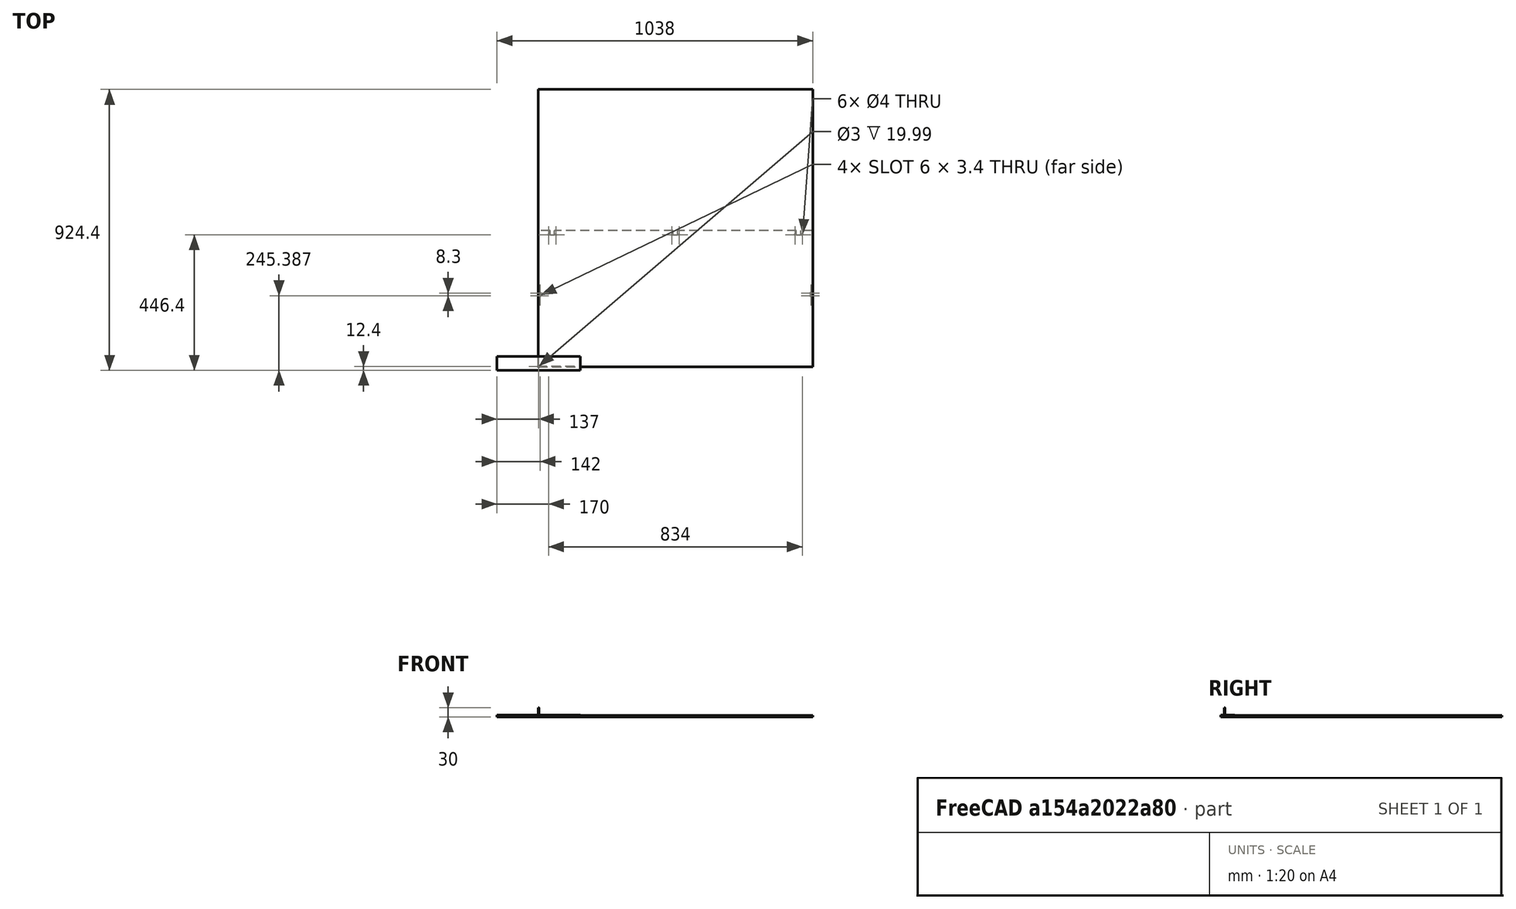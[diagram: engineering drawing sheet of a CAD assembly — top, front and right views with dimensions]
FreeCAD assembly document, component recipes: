
FREECAD ASSEMBLY — COMPONENT RECIPES ("composit_stand12_PP_cut")

This assembly document has 2 components, labeled P0..P1 below (a component is one placed body or linked part). 0 of them carry a construction recipe — the FreeCAD feature program that regenerates the part from scratch, quoted from this document or its linked companion documents; the rest are supplied as boundary geometry only. No exploded tour is included for this assembly.
COMPONENT P0 — geometry summary ("dropper_fix_PP"; no construction recipe available for this part):
  bounding box: 272.0 x 43.4 x 5.0 mm
  tessellated surface: 4,156 triangles
  volume: 51338 mm^3 (87% of its bounding box)
  symmetry: mirror-symmetric across its x mid-plane
COMPONENT P1 — geometry summary ("door_plexiglass"; no construction recipe available for this part):
  bounding box: 911.0 x 447.1 x 4.0 mm
  tessellated surface: 1,824 triangles
  volume: 1626175 mm^3 (100% of its bounding box)
  symmetry: 2-fold rotationally symmetric about the x axis; 2-fold rotationally symmetric about the y axis; 2-fold rotationally symmetric about the z axis; mirror-symmetric across its x mid-plane, y mid-plane, z mid-plane
PROVENANCE & LICENSES
A FreeCAD (.FCStd) document from a public repository crawl; recipes are the document's own serialized feature recipes (and, for linked parts, companion documents' recipes).
License: as declared in the source repository (recorded in the dataset sidecar).
